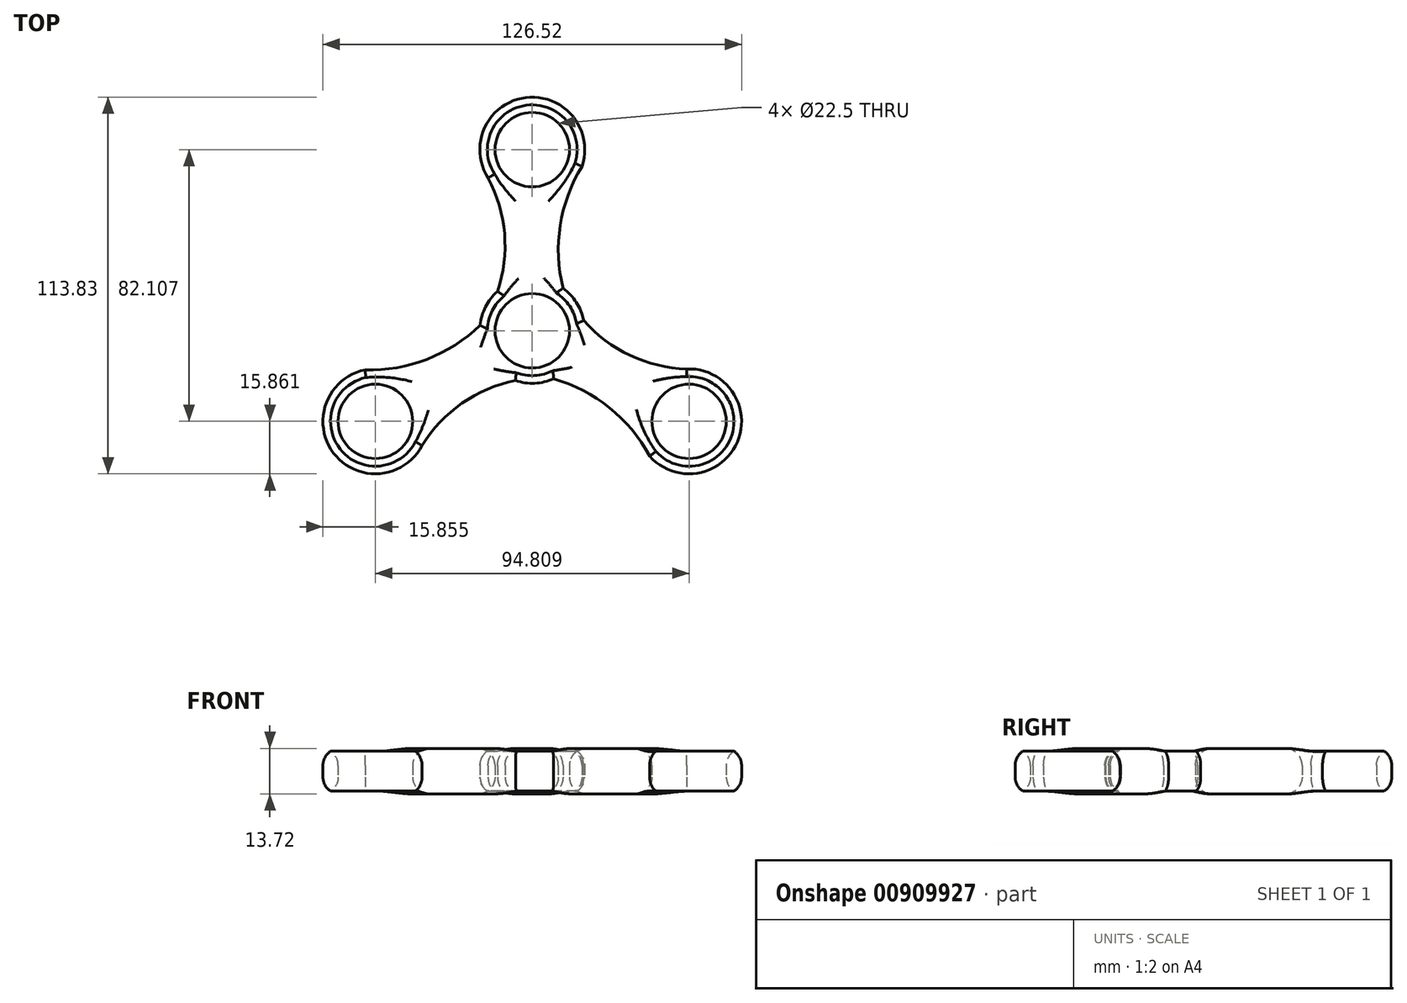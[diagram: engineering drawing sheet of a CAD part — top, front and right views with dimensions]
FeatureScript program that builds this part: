
annotation { "Feature Type Name" : "Feature", "Feature Type Description" : "" }
export const myFeature = defineFeature(function(context is Context, id is Id, definition is map)
    precondition{}
    {
        {
            var Q0;
            Q0=qCreatedBy(makeId("Top.planeOp"),FACE);
            var sketch = newSketch(context, id + "F0", { "sketchPlane" : qUnion([Q0])});
            skCircle(sketch, "E0", {"center": v(0, 0) * mm, "radius": 11.25 * mm});
            skArc(sketch, "E1", {"start": v(-10.5, 11.89) * mm, "mid": v(-14.1, 7.26) * mm, "end": v(-15.77, 1.64) * mm});
            skCircle(sketch, "E2", {"center": v(0, 54.74) * mm, "radius": 11.25 * mm});
            skCircle(sketch, "E3", {"center": v(0, 54.74) * mm, "radius": 15.86 * mm});
            skCircle(sketch, "E4.1.0", {"center": v(-47.4, -27.37) * mm, "radius": 11.25 * mm});
            skCircle(sketch, "E4.1.1", {"center": v(-47.4, -27.37) * mm, "radius": 15.86 * mm});
            skCircle(sketch, "E4.2.0", {"center": v(47.4, -27.37) * mm, "radius": 11.25 * mm});
            skCircle(sketch, "E4.2.1", {"center": v(47.4, -27.37) * mm, "radius": 15.86 * mm});
            skArc(sketch, "E5", {"start": v(-10.5, 11.89) * mm, "mid": v(-8.37, 29.33) * mm, "end": v(-13.35, 46.18) * mm});
            skArc(sketch, "E6", {"start": v(15.02, 49.66) * mm, "mid": v(8.45, 31.83) * mm, "end": v(9.3, 12.84) * mm});
            skArc(sketch, "E7.1.0", {"start": v(-5.05, -15.03) * mm, "mid": v(-21.22, -21.91) * mm, "end": v(-33.32, -34.65) * mm});
            skArc(sketch, "E7.1.1", {"start": v(-50.51, -11.82) * mm, "mid": v(-31.79, -8.6) * mm, "end": v(-15.77, 1.64) * mm});
            skArc(sketch, "E7.2.0", {"start": v(15.54, 3.15) * mm, "mid": v(29.58, -7.42) * mm, "end": v(46.66, -11.53) * mm});
            skArc(sketch, "E7.2.1", {"start": v(35.5, -37.84) * mm, "mid": v(23.34, -23.23) * mm, "end": v(6.47, -14.48) * mm});
            skArc(sketch, "E8.trimOffspring", {"start": v(-5.05, -15.03) * mm, "mid": v(0.76, -15.84) * mm, "end": v(6.47, -14.48) * mm});
            skArc(sketch, "E9.trimOffspring", {"start": v(15.54, 3.15) * mm, "mid": v(13.34, 8.58) * mm, "end": v(9.3, 12.84) * mm});
            skSolve(sketch);
        }
        {
            var Q0;
            Q0=makeQuery(id+"F0.imprint","IMPRINT",FACE,{"disambiguationData":[TD([[makeQuery(id+"F0.imprint","IMPRINT",EDGE,{"derivedFrom":sQuery(id+"F0.wireOp",EDGE,"E0")}),-1.0]])]});
            var Q1;
            Q1=makeQuery(id+"F0.imprint","IMPRINT",FACE,{"disambiguationData":[TD([[makeQuery(id+"F0.imprint","IMPRINT",EDGE,{"derivedFrom":sQuery(id+"F0.wireOp",EDGE,"E2")}),-1.0]])]});
            var Q2;
            Q2=makeQuery(id+"F0.imprint","IMPRINT",FACE,{"disambiguationData":[TD([[makeQuery(id+"F0.imprint","IMPRINT",EDGE,{"derivedFrom":sQuery(id+"F0.wireOp",EDGE,"E4.2.0")}),-1.0]])]});
            var Q3;
            Q3=makeQuery(id+"F0.imprint","IMPRINT",FACE,{"disambiguationData":[TD([[makeQuery(id+"F0.imprint","IMPRINT",EDGE,{"derivedFrom":sQuery(id+"F0.wireOp",EDGE,"E4.1.0")}),-1.0]])]});
            extrude(context, id + "F1", {"entities" : qUnion([Q0, Q1, Q2, Q3]), "depth" : 13.72 * mm, "offsetDistance" : 25.4 * mm});
        }
        {
            var Q0;
            Q0=makeQuery(id+"F1.opExtrude","CAP_FACE",FACE,{"disambiguationData":[OSD([sQuery(id+"F0.wireOp",EDGE,"E0"),sQuery(id+"F0.wireOp",EDGE,"E1"),sQuery(id+"F0.wireOp",EDGE,"E2"),sQuery(id+"F0.wireOp",EDGE,"E3"),sQuery(id+"F0.wireOp",EDGE,"E4.1.0"),sQuery(id+"F0.wireOp",EDGE,"E4.1.1"),sQuery(id+"F0.wireOp",EDGE,"E4.2.0"),sQuery(id+"F0.wireOp",EDGE,"E4.2.1"),sQuery(id+"F0.wireOp",EDGE,"E5"),sQuery(id+"F0.wireOp",EDGE,"E6"),sQuery(id+"F0.wireOp",EDGE,"E7.1.0"),sQuery(id+"F0.wireOp",EDGE,"E7.1.1"),sQuery(id+"F0.wireOp",EDGE,"E7.2.0"),sQuery(id+"F0.wireOp",EDGE,"E7.2.1"),sQuery(id+"F0.wireOp",EDGE,"E8.trimOffspring"),sQuery(id+"F0.wireOp",EDGE,"E9.trimOffspring")])],"isStart":false});
            fillet(context, id + "F2", {"entities" : qUnion([Q0]), "radius" : 5.08 * mm, "tangentPropagation" : true, "allowEdgeOverflow" : false});
        }
        {
            var Q0;
            Q0=makeQuery(id+"F1.opExtrude","CAP_FACE",FACE,{"disambiguationData":[OSD([sQuery(id+"F0.wireOp",EDGE,"E0"),sQuery(id+"F0.wireOp",EDGE,"E1"),sQuery(id+"F0.wireOp",EDGE,"E2"),sQuery(id+"F0.wireOp",EDGE,"E3"),sQuery(id+"F0.wireOp",EDGE,"E4.1.0"),sQuery(id+"F0.wireOp",EDGE,"E4.1.1"),sQuery(id+"F0.wireOp",EDGE,"E4.2.0"),sQuery(id+"F0.wireOp",EDGE,"E4.2.1"),sQuery(id+"F0.wireOp",EDGE,"E5"),sQuery(id+"F0.wireOp",EDGE,"E6"),sQuery(id+"F0.wireOp",EDGE,"E7.1.0"),sQuery(id+"F0.wireOp",EDGE,"E7.1.1"),sQuery(id+"F0.wireOp",EDGE,"E7.2.0"),sQuery(id+"F0.wireOp",EDGE,"E7.2.1"),sQuery(id+"F0.wireOp",EDGE,"E8.trimOffspring"),sQuery(id+"F0.wireOp",EDGE,"E9.trimOffspring")])],"isStart":true});
            fillet(context, id + "F3", {"entities" : qUnion([Q0]), "radius" : 5.08 * mm, "tangentPropagation" : true, "allowEdgeOverflow" : false});
        }
    });
